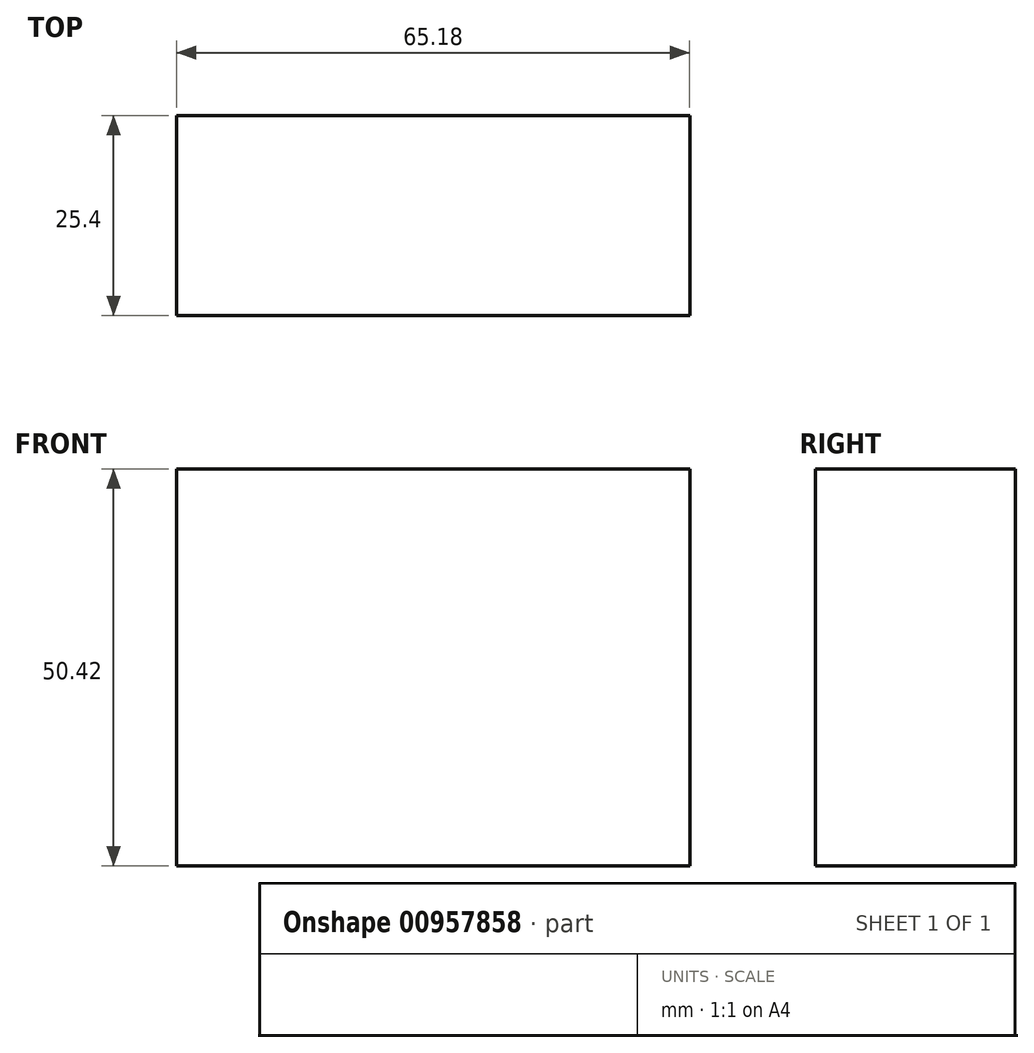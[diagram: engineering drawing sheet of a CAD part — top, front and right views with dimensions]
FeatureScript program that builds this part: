
annotation { "Feature Type Name" : "Feature", "Feature Type Description" : "" }
export const myFeature = defineFeature(function(context is Context, id is Id, definition is map)
    precondition{}
    {
        {
            var Q0;
            Q0=qCreatedBy(makeId("Front.planeOp"),FACE);
            var sketch = newSketch(context, id + "F0", { "sketchPlane" : qUnion([Q0])});
            skLineSegment(sketch, "E0.bottom", {"start": v(-148.47, 65.34) * mm, "end": v(-83.29, 65.34) * mm});
            skLineSegment(sketch, "E0.top", {"start": v(-148.47, 14.92) * mm, "end": v(-83.29, 14.92) * mm});
            skLineSegment(sketch, "E0.left", {"start": v(-148.47, 65.34) * mm, "end": v(-148.47, 14.92) * mm});
            skLineSegment(sketch, "E0.right", {"start": v(-83.29, 65.34) * mm, "end": v(-83.29, 14.92) * mm});
            skSolve(sketch);
        }
        {
            var Q0;
            Q0 = qSketchRegion(id + "F0", true);
            extrude(context, id + "F1", {"entities" : qUnion([Q0]), "depth" : 25.4 * mm, "offsetDistance" : 25.4 * mm});
        }
    });
